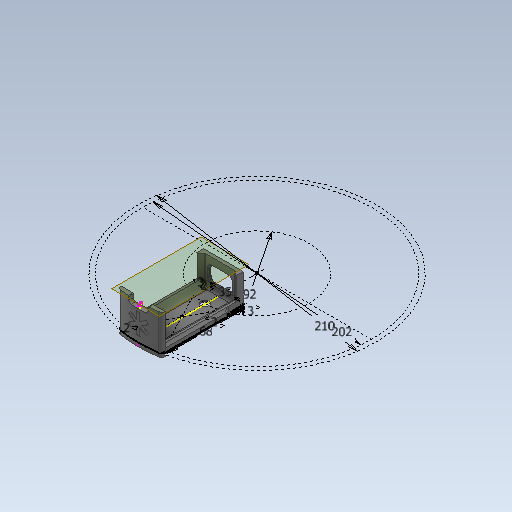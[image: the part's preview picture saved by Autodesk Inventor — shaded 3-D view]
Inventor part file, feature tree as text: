
AUTODESK INVENTOR PART (.ipt)
format: ipt  version: 2020 (Build 240168000, 168)  size: 657,920 bytes
history: native  units: mm
features: projected_geometry x30, extrude x16, sketch x11, fillet x10, other x6, chamfer x2
ambient origin geometry x8: Origin, YZ Plane, XZ Plane, XY Plane, X Axis, Y Axis, Z Axis, Center Point
bodies: Body1 (feature_tree)
feature tree (75):
  other  "Твердое тело1"
  sketch  "Эскиз1"
  extrude  "Выдавливание3"  Depth=202.0mm
  other  "РабПлоскость1"
  extrude  "Выдавливание1"  Depth=35.0mm
  other  "РабПлоскость2"
  sketch  "Эскиз2"
  extrude  "Выдавливание4"  Depth=68.0mm
  extrude  "Выдавливание5"  Depth=2.0mm
  sketch  "Эскиз4"
  extrude  "Выдавливание6"  Depth=2.0mm
  extrude  "Выдавливание7"  Depth=3.0mm
  other  "РабПлоскость3"
  extrude  "Выдавливание8"  Depth=3.0mm
  other  "РабПлоскость4"
  extrude  "Выдавливание9"  Depth=210.0mm
  sketch  "Эскиз8"
  extrude  "Выдавливание10"  Depth=20.0mm TaperAngle=0.0deg
  fillet  "Сопряжение1"  Radius=1.5mm
  fillet  "Сопряжение2"  Radius=28.0mm
  fillet  "Сопряжение3"  Radius=7.0mm
  fillet  "Сопряжение4"  Radius=20.0mm
  fillet  "Сопряжение5"  Radius=13.0mm
  extrude  "Выдавливание11"  Depth=5.0mm
  extrude  "Выдавливание12"  Depth=3.0mm
  fillet  "Сопряжение6"  Radius=10.0mm
  extrude  "Выдавливание13"  Depth=84.0mm
  chamfer  "Фаска1"  Distance=5.0mm
  fillet  "Сопряжение7"  Radius=52.0mm
  sketch  "Эскиз10"
  other  "РабПлоскость5"
  extrude  "Выдавливание14"  Depth=5.0mm TaperAngle=0.0deg
  fillet  "Сопряжение8"  Radius=35.0mm
  extrude  "Выдавливание15"  Depth=18.0mm
  fillet  "Сопряжение9"  Radius=3.0mm
  extrude  "Выдавливание16"  Depth=30.0mm TaperAngle=360.0deg
  fillet  "Сопряжение10"  Radius=0.5mm
  extrude  "Выдавливание17"  TaperAngle=0.0deg  [1 undecoded]
  chamfer  "Фаска2"  Distance=8.0mm
  projected_geometry  "Спроецированная петля1"
  projected_geometry  "Спроецированная петля7"
  projected_geometry  "Спроецированная петля8"
  sketch  "Эскиз3"
  projected_geometry  "Спроецированная петля9"
  projected_geometry  "Спроецированная петля10"
  projected_geometry  "Спроецированная петля11"
  projected_geometry  "Спроецированная петля12"
  sketch  "Эскиз5"
  projected_geometry  "Спроецированная петля13"
  projected_geometry  "Спроецированная петля14"
  projected_geometry  "Спроецированная петля15"
  projected_geometry  "Спроецированная петля16"
  projected_geometry  "Спроецированная петля17"
  sketch  "Эскиз6"
  projected_geometry  "Спроецированная петля18"
  projected_geometry  "Спроецированная петля19"
  projected_geometry  "Спроецированная петля20"
  projected_geometry  "Спроецированная петля21"
  projected_geometry  "Спроецированная петля22"
  projected_geometry  "Спроецированная петля23"
  projected_geometry  "Спроецированная петля24"
  projected_geometry  "Спроецированная петля25"
  projected_geometry  "Спроецированная петля26"
  projected_geometry  "Спроецированная петля27"
  projected_geometry  "Спроецированная петля28"
  sketch  "Эскиз9"
  projected_geometry  "Спроецированная петля29"
  projected_geometry  "Спроецированная петля30"
  sketch  "Эскиз11"
  projected_geometry  "Спроецированная петля31"
  projected_geometry  "Спроецированная петля32"
  projected_geometry  "Спроецированная петля33"
  sketch  "Эскиз12"
  projected_geometry  "Спроецированная петля34"
  projected_geometry  "Спроецированная петля35"
note: 1 required parameter value undecoded (feature->parameter linkage not recoverable at this tier; creation-order binding heuristic only, values carry confidence <= 0.55)
